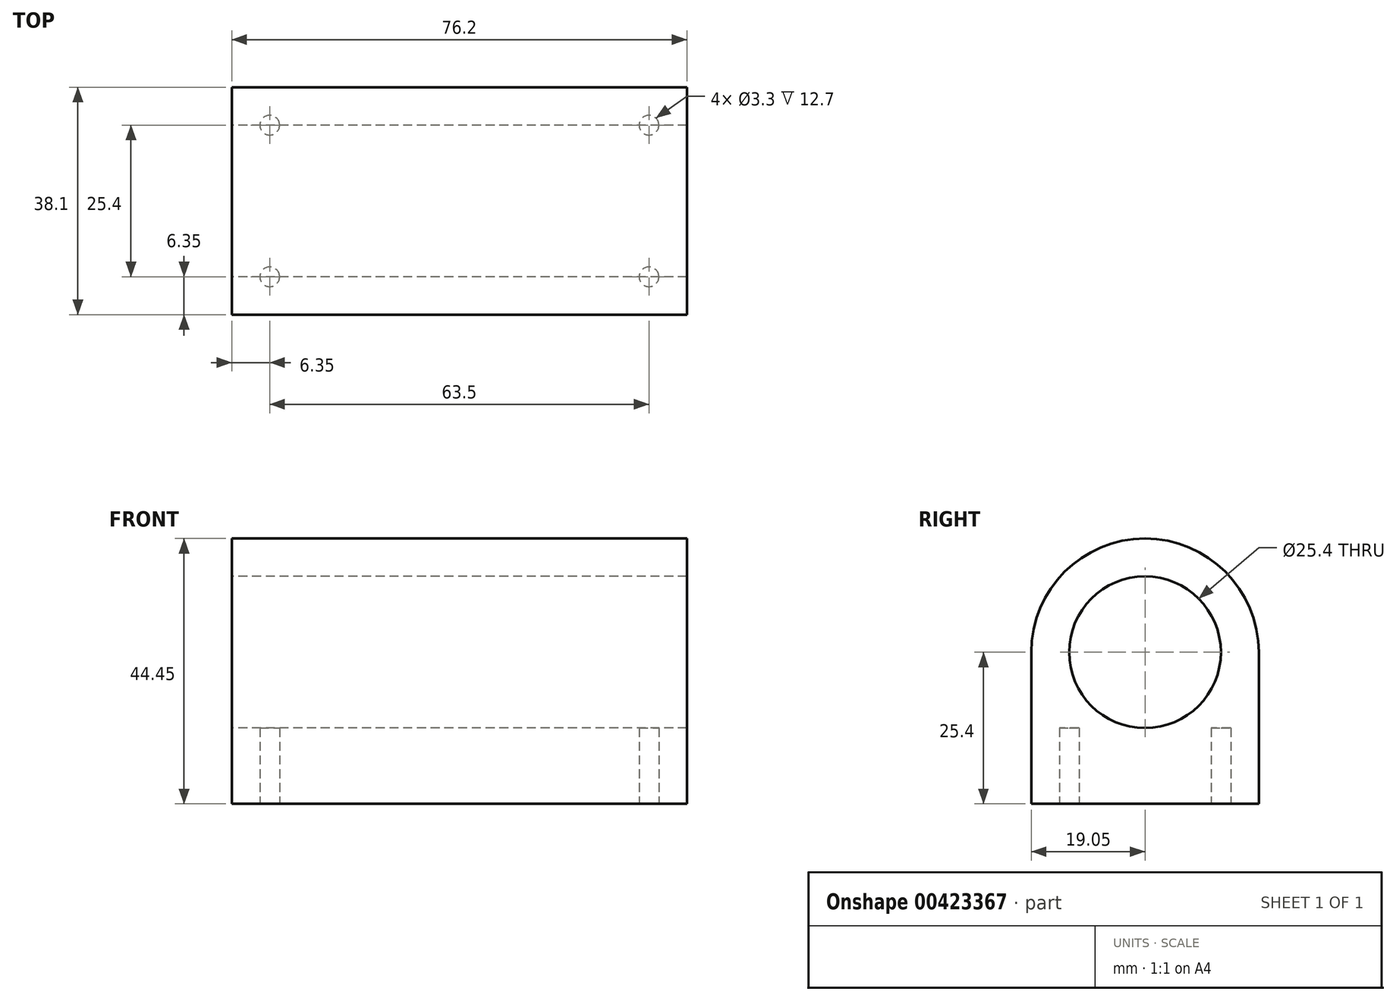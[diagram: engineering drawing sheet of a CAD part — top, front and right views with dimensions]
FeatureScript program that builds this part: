
annotation { "Feature Type Name" : "Feature", "Feature Type Description" : "" }
export const myFeature = defineFeature(function(context is Context, id is Id, definition is map)
    precondition{}
    {
        {
            var Q0;
            Q0=qCreatedBy(makeId("Right.planeOp"),FACE);
            var sketch = newSketch(context, id + "F0", { "sketchPlane" : qUnion([Q0])});
            skCircle(sketch, "E0", {"center": v(0, 0) * mm, "radius": 12.7 * mm});
            skCircle(sketch, "E1", {"center": v(0, 0) * mm, "radius": 19.05 * mm});
            skLineSegment(sketch, "E2.bottom", {"start": v(-19.05, 0) * mm, "end": v(19.05, 0) * mm});
            skLineSegment(sketch, "E2.top", {"start": v(-19.05, -25.4) * mm, "end": v(19.05, -25.4) * mm});
            skLineSegment(sketch, "E2.left", {"start": v(-19.05, 0) * mm, "end": v(-19.05, -25.4) * mm});
            skLineSegment(sketch, "E2.right", {"start": v(19.05, 0) * mm, "end": v(19.05, -25.4) * mm});
            skSolve(sketch);
        }
        {
            var Q0;
            Q0 = qSketchRegion(id + "F0", true);
            extrude(context, id + "F1", {"entities" : qUnion([Q0]), "endBound" : BoundingType.SYMMETRIC, "depth" : 76.2 * mm});
        }
        {
            var Q0;
            Q0=makeQuery(id+"F1.opExtrude","SWEPT_FACE",FACE,{"disambiguationData":[OSD([sQuery(id+"F0.wireOp",EDGE,"E2.top")])]});
            var sketch = newSketch(context, id + "F2", { "sketchPlane" : qUnion([Q0])});
            skLineSegment(sketch, "E3.bottom", {"start": v(-31.75, 12.7) * mm, "end": v(31.75, 12.7) * mm, "construction": true});
            skLineSegment(sketch, "E3.top", {"start": v(-31.75, -12.7) * mm, "end": v(31.75, -12.7) * mm, "construction": true});
            skLineSegment(sketch, "E3.left", {"start": v(-31.75, 12.7) * mm, "end": v(-31.75, -12.7) * mm, "construction": true});
            skLineSegment(sketch, "E3.right", {"start": v(31.75, 12.7) * mm, "end": v(31.75, -12.7) * mm, "construction": true});
            skCircle(sketch, "E4", {"center": v(-31.75, 12.7) * mm, "radius": 1.65 * mm});
            skCircle(sketch, "E5", {"center": v(-31.75, -12.7) * mm, "radius": 1.65 * mm});
            skCircle(sketch, "E6", {"center": v(31.75, -12.7) * mm, "radius": 1.65 * mm});
            skCircle(sketch, "E7", {"center": v(31.75, 12.7) * mm, "radius": 1.65 * mm});
            skSolve(sketch);
        }
        {
            var Q0;
            Q0 = qSketchRegion(id + "F2", true);
            extrude(context, id + "F3", {"entities" : qUnion([Q0]), "operationType" : NewBodyOperationType.REMOVE, "oppositeDirection" : true, "depth" : 12.7 * mm});
        }
    });
